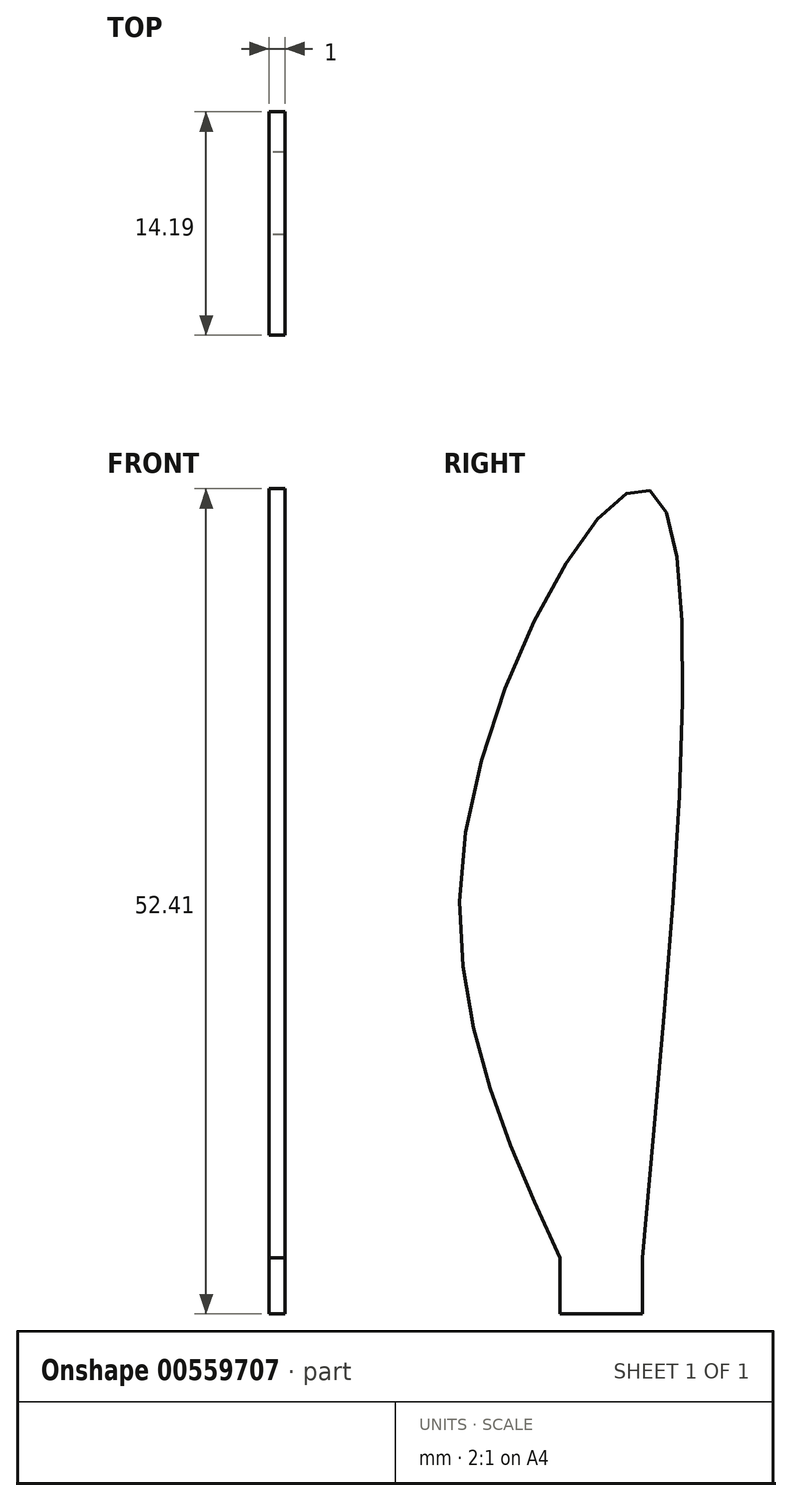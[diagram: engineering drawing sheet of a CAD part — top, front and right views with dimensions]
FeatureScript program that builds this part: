
annotation { "Feature Type Name" : "Feature", "Feature Type Description" : "" }
export const myFeature = defineFeature(function(context is Context, id is Id, definition is map)
    precondition{}
    {
        {
            var Q0;
            Q0=qCreatedBy(makeId("Right.planeOp"),FACE);
            var sketch = newSketch(context, id + "F0", { "sketchPlane" : qUnion([Q0])});
            skFitSpline(sketch, "E0", {"points": [v(0, 0) * mm, v(0, 48.86) * mm, v(-11.19, 27.34) * mm, v(-5.24, 0) * mm], "startDerivative": vector(16.41, 179.6) * mm, "endDerivative": vector(37.47, -81.65) * mm});
            skLineSegment(sketch, "E1", {"start": v(0, 0) * mm, "end": v(-5.24, 0) * mm});
            skLineSegment(sketch, "E2", {"start": v(0, 0) * mm, "end": v(0, -3.54) * mm});
            skLineSegment(sketch, "E3", {"start": v(0, -3.54) * mm, "end": v(-5.24, -3.54) * mm});
            skLineSegment(sketch, "E4", {"start": v(-5.24, -3.54) * mm, "end": v(-5.24, 0) * mm});
            skSolve(sketch);
        }
        {
            var Q0;
            Q0=makeQuery(id+"F0.imprint","IMPRINT",FACE,{"disambiguationData":[TD([[makeQuery(id+"F0.imprint","IMPRINT",EDGE,{"derivedFrom":sQuery(id+"F0.wireOp",EDGE,"E0")}),1.0]])]});
            var Q1;
            Q1=makeQuery(id+"F0.imprint","IMPRINT",FACE,{"disambiguationData":[TD([[makeQuery(id+"F0.imprint","IMPRINT",EDGE,{"derivedFrom":sQuery(id+"F0.wireOp",EDGE,"E1")}),1.0]])]});
            extrude(context, id + "F1", {"entities" : qUnion([Q0, Q1]), "depth" : 1 * mm, "offsetDistance" : 25 * mm});
        }
    });
